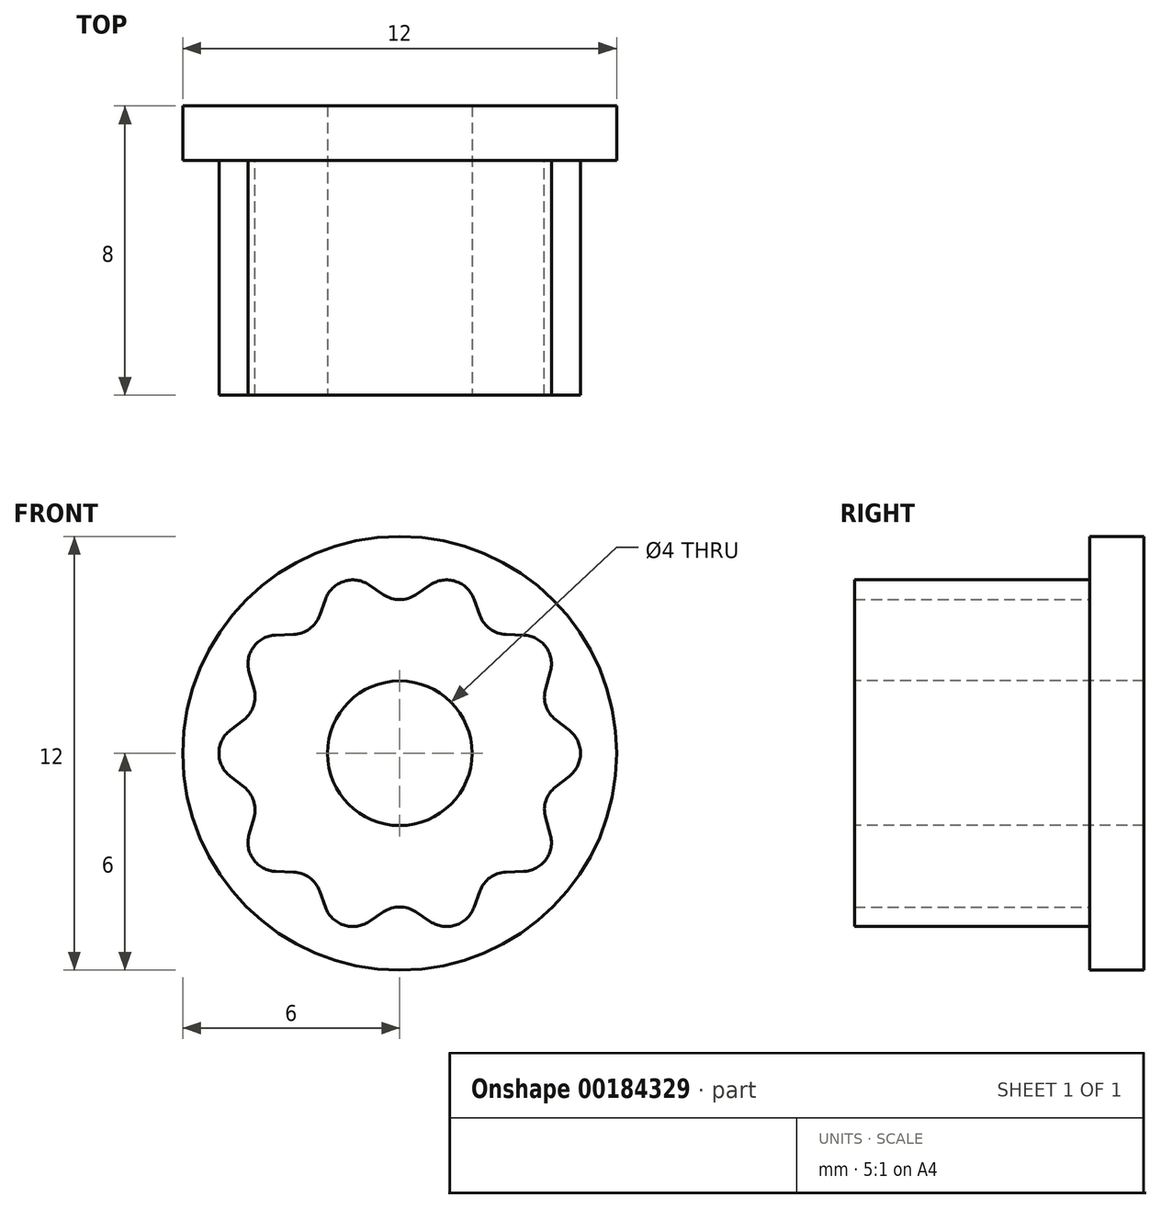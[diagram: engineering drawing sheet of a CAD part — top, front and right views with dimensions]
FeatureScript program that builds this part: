
annotation { "Feature Type Name" : "Feature", "Feature Type Description" : "" }
export const myFeature = defineFeature(function(context is Context, id is Id, definition is map)
    precondition{}
    {
        {
            var Q0;
            Q0=qCreatedBy(makeId("Front.planeOp"),FACE);
            var sketch = newSketch(context, id + "F0", { "sketchPlane" : qUnion([Q0])});
            skCircle(sketch, "E0", {"center": v(0, 0) * mm, "radius": 5.5 * mm, "construction": true});
            skCircle(sketch, "E1", {"center": v(0, 0) * mm, "radius": 4.09 * mm, "construction": true});
            skLineSegment(sketch, "E2", {"start": v(0, 0) * mm, "end": v(0, 5.5) * mm, "construction": true});
            skLineSegment(sketch, "E3", {"start": v(0, 0) * mm, "end": v(1.7, 5.23) * mm, "construction": true});
            skLineSegment(sketch, "E4", {"start": v(0, 0) * mm, "end": v(3.23, 4.45) * mm, "construction": true});
            skLineSegment(sketch, "E5", {"start": v(0, 0) * mm, "end": v(4.45, 3.23) * mm, "construction": true});
            skLineSegment(sketch, "E6", {"start": v(0, 0) * mm, "end": v(5.23, 1.7) * mm, "construction": true});
            skLineSegment(sketch, "E7", {"start": v(0, 4.09) * mm, "end": v(0.85, 4.66) * mm, "construction": true});
            skLineSegment(sketch, "E8", {"start": v(2.22, 3.81) * mm, "end": v(2.05, 4.27) * mm});
            skLineSegment(sketch, "E9", {"start": v(2.94, 3.29) * mm, "end": v(3.43, 3.27) * mm});
            skLineSegment(sketch, "E10", {"start": v(4.17, 2.25) * mm, "end": v(3.89, 1.26) * mm, "construction": true});
            skPoint(sketch, "E11.visualSharp", {"position": v(1.7, 5.23) * mm});
            skArc(sketch, "E11.filletArc", {"start": v(2.05, 4.27) * mm, "mid": v(1.55, 4.76) * mm, "end": v(0.85, 4.66) * mm});
            skPoint(sketch, "E12.visualSharp", {"position": v(2.4, 3.3) * mm});
            skArc(sketch, "E12.filletArc", {"start": v(2.22, 3.81) * mm, "mid": v(2.5, 3.44) * mm, "end": v(2.94, 3.29) * mm});
            skPoint(sketch, "E13.visualSharp", {"position": v(4.45, 3.23) * mm});
            skArc(sketch, "E13.filletArc", {"start": v(4.17, 2.25) * mm, "mid": v(4.05, 2.94) * mm, "end": v(3.43, 3.27) * mm});
            skArc(sketch, "E14.1.0", {"start": v(-0.85, 4.66) * mm, "mid": v(-1.55, 4.76) * mm, "end": v(-2.05, 4.27) * mm});
            skLineSegment(sketch, "E14.1.1", {"start": v(-0.45, 4.39) * mm, "end": v(-0.85, 4.66) * mm});
            skArc(sketch, "E14.1.2", {"start": v(-0.45, 4.39) * mm, "mid": v(0, 4.25) * mm, "end": v(0.45, 4.39) * mm});
            skLineSegment(sketch, "E14.1.3", {"start": v(0.45, 4.39) * mm, "end": v(0.85, 4.66) * mm});
            skArc(sketch, "E14.2.0", {"start": v(-3.43, 3.27) * mm, "mid": v(-4.05, 2.94) * mm, "end": v(-4.17, 2.25) * mm});
            skLineSegment(sketch, "E14.2.1", {"start": v(-2.94, 3.29) * mm, "end": v(-3.43, 3.27) * mm});
            skArc(sketch, "E14.2.2", {"start": v(-2.94, 3.29) * mm, "mid": v(-2.5, 3.44) * mm, "end": v(-2.22, 3.81) * mm});
            skLineSegment(sketch, "E14.2.3", {"start": v(-2.22, 3.81) * mm, "end": v(-2.05, 4.27) * mm});
            skArc(sketch, "E14.3.0", {"start": v(-4.7, 0.63) * mm, "mid": v(-5, 0) * mm, "end": v(-4.7, -0.63) * mm});
            skLineSegment(sketch, "E14.3.1", {"start": v(-4.3, 0.93) * mm, "end": v(-4.7, 0.63) * mm});
            skArc(sketch, "E14.3.2", {"start": v(-4.3, 0.93) * mm, "mid": v(-4.04, 1.31) * mm, "end": v(-4.03, 1.78) * mm});
            skLineSegment(sketch, "E14.3.3", {"start": v(-4.03, 1.78) * mm, "end": v(-4.17, 2.25) * mm});
            skArc(sketch, "E14.4.0", {"start": v(-4.17, -2.25) * mm, "mid": v(-4.05, -2.94) * mm, "end": v(-3.43, -3.27) * mm});
            skLineSegment(sketch, "E14.4.1", {"start": v(-4.03, -1.78) * mm, "end": v(-4.17, -2.25) * mm});
            skArc(sketch, "E14.4.2", {"start": v(-4.03, -1.78) * mm, "mid": v(-4.04, -1.31) * mm, "end": v(-4.3, -0.93) * mm});
            skLineSegment(sketch, "E14.4.3", {"start": v(-4.3, -0.93) * mm, "end": v(-4.7, -0.63) * mm});
            skArc(sketch, "E14.5.0", {"start": v(-2.05, -4.27) * mm, "mid": v(-1.55, -4.76) * mm, "end": v(-0.85, -4.66) * mm});
            skLineSegment(sketch, "E14.5.1", {"start": v(-2.22, -3.81) * mm, "end": v(-2.05, -4.27) * mm});
            skArc(sketch, "E14.5.2", {"start": v(-2.22, -3.81) * mm, "mid": v(-2.5, -3.44) * mm, "end": v(-2.94, -3.29) * mm});
            skLineSegment(sketch, "E14.5.3", {"start": v(-2.94, -3.29) * mm, "end": v(-3.43, -3.27) * mm});
            skArc(sketch, "E14.6.0", {"start": v(0.85, -4.66) * mm, "mid": v(1.55, -4.76) * mm, "end": v(2.05, -4.27) * mm});
            skLineSegment(sketch, "E14.6.1", {"start": v(0.45, -4.39) * mm, "end": v(0.85, -4.66) * mm});
            skArc(sketch, "E14.6.2", {"start": v(0.45, -4.39) * mm, "mid": v(0, -4.25) * mm, "end": v(-0.45, -4.39) * mm});
            skLineSegment(sketch, "E14.6.3", {"start": v(-0.45, -4.39) * mm, "end": v(-0.85, -4.66) * mm});
            skArc(sketch, "E14.7.0", {"start": v(3.43, -3.27) * mm, "mid": v(4.05, -2.94) * mm, "end": v(4.17, -2.25) * mm});
            skLineSegment(sketch, "E14.7.1", {"start": v(2.94, -3.29) * mm, "end": v(3.43, -3.27) * mm});
            skArc(sketch, "E14.7.2", {"start": v(2.94, -3.29) * mm, "mid": v(2.5, -3.44) * mm, "end": v(2.22, -3.81) * mm});
            skLineSegment(sketch, "E14.7.3", {"start": v(2.22, -3.81) * mm, "end": v(2.05, -4.27) * mm});
            skArc(sketch, "E14.8.0", {"start": v(4.7, -0.63) * mm, "mid": v(5, 0) * mm, "end": v(4.7, 0.63) * mm});
            skLineSegment(sketch, "E14.8.1", {"start": v(4.3, -0.93) * mm, "end": v(4.7, -0.63) * mm});
            skArc(sketch, "E14.8.2", {"start": v(4.3, -0.93) * mm, "mid": v(4.04, -1.31) * mm, "end": v(4.03, -1.78) * mm});
            skLineSegment(sketch, "E14.8.3", {"start": v(4.03, -1.78) * mm, "end": v(4.17, -2.25) * mm});
            skLineSegment(sketch, "E14.9.1", {"start": v(4.03, 1.78) * mm, "end": v(4.17, 2.25) * mm});
            skArc(sketch, "E14.9.2", {"start": v(4.03, 1.78) * mm, "mid": v(4.04, 1.31) * mm, "end": v(4.3, 0.93) * mm});
            skLineSegment(sketch, "E14.9.3", {"start": v(4.3, 0.93) * mm, "end": v(4.7, 0.63) * mm});
            skCircle(sketch, "E15", {"center": v(0, 0) * mm, "radius": 6 * mm});
            skSolve(sketch);
        }
        {
            var Q0;
            Q0=makeQuery(id+"F0.imprint","IMPRINT",FACE,{"disambiguationData":[TD([[makeQuery(id+"F0.imprint","IMPRINT",EDGE,{"derivedFrom":sQuery(id+"F0.wireOp",EDGE,"E8")}),1.0]])]});
            extrude(context, id + "F1", {"entities" : qUnion([Q0]), "depth" : 6.5 * mm});
        }
        {
            var Q0;
            Q0=makeQuery(id+"F0.imprint","IMPRINT",FACE,{"disambiguationData":[TD([[makeQuery(id+"F0.imprint","IMPRINT",EDGE,{"derivedFrom":sQuery(id+"F0.wireOp",EDGE,"E8")}),-1.0]])]});
            var Q1;
            Q1=makeQuery(id+"F0.imprint","IMPRINT",FACE,{"disambiguationData":[TD([[makeQuery(id+"F0.imprint","IMPRINT",EDGE,{"derivedFrom":sQuery(id+"F0.wireOp",EDGE,"E8")}),1.0]])]});
            extrude(context, id + "F2", {"entities" : qUnion([Q0, Q1]), "operationType" : NewBodyOperationType.ADD, "oppositeDirection" : true, "depth" : 1.5 * mm});
        }
        {
            var Q0;
            Q0=makeQuery(id+"F1.opExtrude","CAP_FACE",FACE,{"disambiguationData":[OSD([sQuery(id+"F0.wireOp",EDGE,"E8"),sQuery(id+"F0.wireOp",EDGE,"E9"),sQuery(id+"F0.wireOp",EDGE,"E11.filletArc"),sQuery(id+"F0.wireOp",EDGE,"E12.filletArc"),sQuery(id+"F0.wireOp",EDGE,"E14.1.0"),sQuery(id+"F0.wireOp",EDGE,"E14.1.1"),sQuery(id+"F0.wireOp",EDGE,"E14.1.2"),sQuery(id+"F0.wireOp",EDGE,"E14.1.3"),sQuery(id+"F0.wireOp",EDGE,"E14.2.0"),sQuery(id+"F0.wireOp",EDGE,"E14.2.1"),sQuery(id+"F0.wireOp",EDGE,"E14.2.2"),sQuery(id+"F0.wireOp",EDGE,"E14.2.3"),sQuery(id+"F0.wireOp",EDGE,"E14.3.0"),sQuery(id+"F0.wireOp",EDGE,"E14.3.1"),sQuery(id+"F0.wireOp",EDGE,"E14.3.2"),sQuery(id+"F0.wireOp",EDGE,"E14.3.3"),sQuery(id+"F0.wireOp",EDGE,"E14.4.0"),sQuery(id+"F0.wireOp",EDGE,"E14.4.1"),sQuery(id+"F0.wireOp",EDGE,"E14.4.2"),sQuery(id+"F0.wireOp",EDGE,"E14.4.3"),sQuery(id+"F0.wireOp",EDGE,"E14.5.0"),sQuery(id+"F0.wireOp",EDGE,"E14.5.1"),sQuery(id+"F0.wireOp",EDGE,"E14.5.2"),sQuery(id+"F0.wireOp",EDGE,"E14.5.3"),sQuery(id+"F0.wireOp",EDGE,"E14.6.0"),sQuery(id+"F0.wireOp",EDGE,"E14.6.1"),sQuery(id+"F0.wireOp",EDGE,"E14.6.2"),sQuery(id+"F0.wireOp",EDGE,"E14.6.3"),sQuery(id+"F0.wireOp",EDGE,"E14.7.0"),sQuery(id+"F0.wireOp",EDGE,"E14.7.1"),sQuery(id+"F0.wireOp",EDGE,"E14.7.2"),sQuery(id+"F0.wireOp",EDGE,"E14.7.3"),sQuery(id+"F0.wireOp",EDGE,"E14.8.0"),sQuery(id+"F0.wireOp",EDGE,"E14.8.1"),sQuery(id+"F0.wireOp",EDGE,"E14.8.2"),sQuery(id+"F0.wireOp",EDGE,"E14.8.3"),sQuery(id+"F0.wireOp",EDGE,"E13.filletArc"),sQuery(id+"F0.wireOp",EDGE,"E14.9.1"),sQuery(id+"F0.wireOp",EDGE,"E14.9.2"),sQuery(id+"F0.wireOp",EDGE,"E14.9.3")])],"isStart":false});
            var sketch = newSketch(context, id + "F3", { "sketchPlane" : qUnion([Q0])});
            skPoint(sketch, "E16", {"position": v(0, 0) * mm});
            skSolve(sketch);
        }
        {
            var Q0;
            Q0=sQuery(id+"F3.wireOp",VERTEX,"E16");
            var Q1;
            Q1=makeQuery(id+"F1.opExtrude","SWEPT_BODY",BODY,{"disambiguationData":[OSD([sQuery(id+"F0.wireOp",EDGE,"E8"),sQuery(id+"F0.wireOp",EDGE,"E9"),sQuery(id+"F0.wireOp",EDGE,"E11.filletArc"),sQuery(id+"F0.wireOp",EDGE,"E12.filletArc"),sQuery(id+"F0.wireOp",EDGE,"E14.1.0"),sQuery(id+"F0.wireOp",EDGE,"E14.1.1"),sQuery(id+"F0.wireOp",EDGE,"E14.1.2"),sQuery(id+"F0.wireOp",EDGE,"E14.1.3"),sQuery(id+"F0.wireOp",EDGE,"E14.2.0"),sQuery(id+"F0.wireOp",EDGE,"E14.2.1"),sQuery(id+"F0.wireOp",EDGE,"E14.2.2"),sQuery(id+"F0.wireOp",EDGE,"E14.2.3"),sQuery(id+"F0.wireOp",EDGE,"E14.3.0"),sQuery(id+"F0.wireOp",EDGE,"E14.3.1"),sQuery(id+"F0.wireOp",EDGE,"E14.3.2"),sQuery(id+"F0.wireOp",EDGE,"E14.3.3"),sQuery(id+"F0.wireOp",EDGE,"E14.4.0"),sQuery(id+"F0.wireOp",EDGE,"E14.4.1"),sQuery(id+"F0.wireOp",EDGE,"E14.4.2"),sQuery(id+"F0.wireOp",EDGE,"E14.4.3"),sQuery(id+"F0.wireOp",EDGE,"E14.5.0"),sQuery(id+"F0.wireOp",EDGE,"E14.5.1"),sQuery(id+"F0.wireOp",EDGE,"E14.5.2"),sQuery(id+"F0.wireOp",EDGE,"E14.5.3"),sQuery(id+"F0.wireOp",EDGE,"E14.6.0"),sQuery(id+"F0.wireOp",EDGE,"E14.6.1"),sQuery(id+"F0.wireOp",EDGE,"E14.6.2"),sQuery(id+"F0.wireOp",EDGE,"E14.6.3"),sQuery(id+"F0.wireOp",EDGE,"E14.7.0"),sQuery(id+"F0.wireOp",EDGE,"E14.7.1"),sQuery(id+"F0.wireOp",EDGE,"E14.7.2"),sQuery(id+"F0.wireOp",EDGE,"E14.7.3"),sQuery(id+"F0.wireOp",EDGE,"E14.8.0"),sQuery(id+"F0.wireOp",EDGE,"E14.8.1"),sQuery(id+"F0.wireOp",EDGE,"E14.8.2"),sQuery(id+"F0.wireOp",EDGE,"E14.8.3"),sQuery(id+"F0.wireOp",EDGE,"E13.filletArc"),sQuery(id+"F0.wireOp",EDGE,"E14.9.1"),sQuery(id+"F0.wireOp",EDGE,"E14.9.2"),sQuery(id+"F0.wireOp",EDGE,"E14.9.3")])]});
            hole(context, id + "F4", {"style" : HoleStyle.SIMPLE, "endStyle" : HoleEndStyle.THROUGH, "holeDiameter" : 4 * mm, "locations" : qUnion([Q0]), "scope" : qUnion([Q1]), "isTappedThrough" : true});
        }
    });
